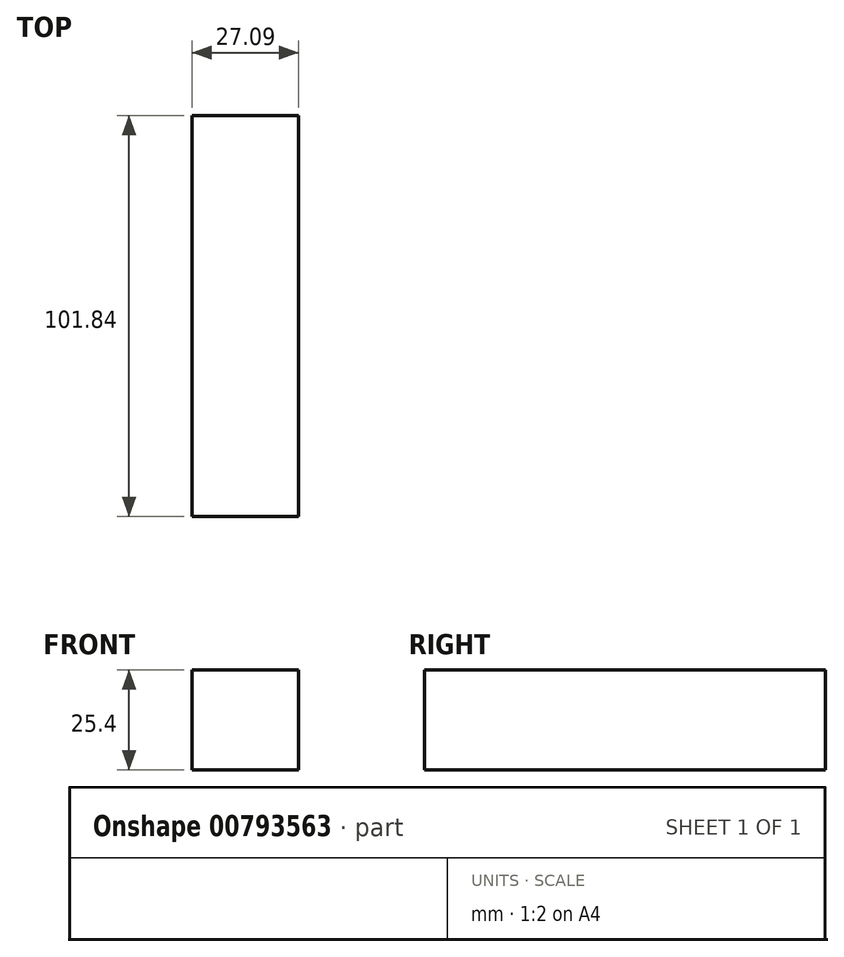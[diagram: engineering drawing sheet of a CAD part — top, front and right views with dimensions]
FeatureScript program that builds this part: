
annotation { "Feature Type Name" : "Feature", "Feature Type Description" : "" }
export const myFeature = defineFeature(function(context is Context, id is Id, definition is map)
    precondition{}
    {
        {
            var Q0;
            Q0=qCreatedBy(makeId("Top.planeOp"),FACE);
            var sketch = newSketch(context, id + "F0", { "sketchPlane" : qUnion([Q0])});
            skLineSegment(sketch, "E0.bottom", {"start": v(-38.26, -62.8) * mm, "end": v(-11.17, -62.8) * mm});
            skLineSegment(sketch, "E0.top", {"start": v(-38.26, 39.04) * mm, "end": v(-11.17, 39.04) * mm});
            skLineSegment(sketch, "E0.left", {"start": v(-38.26, -62.8) * mm, "end": v(-38.26, 39.04) * mm});
            skLineSegment(sketch, "E0.right", {"start": v(-11.17, -62.8) * mm, "end": v(-11.17, 39.04) * mm});
            skSolve(sketch);
        }
        {
            var Q0;
            Q0=makeQuery(id+"F0.imprint","IMPRINT",FACE,{"disambiguationData":[TD([[makeQuery(id+"F0.imprint","IMPRINT",EDGE,{"derivedFrom":sQuery(id+"F0.wireOp",EDGE,"E0.bottom")}),1.0]])]});
            extrude(context, id + "F1", {"entities" : qUnion([Q0]), "depth" : 25.4 * mm, "offsetDistance" : 25.4 * mm});
        }
    });
